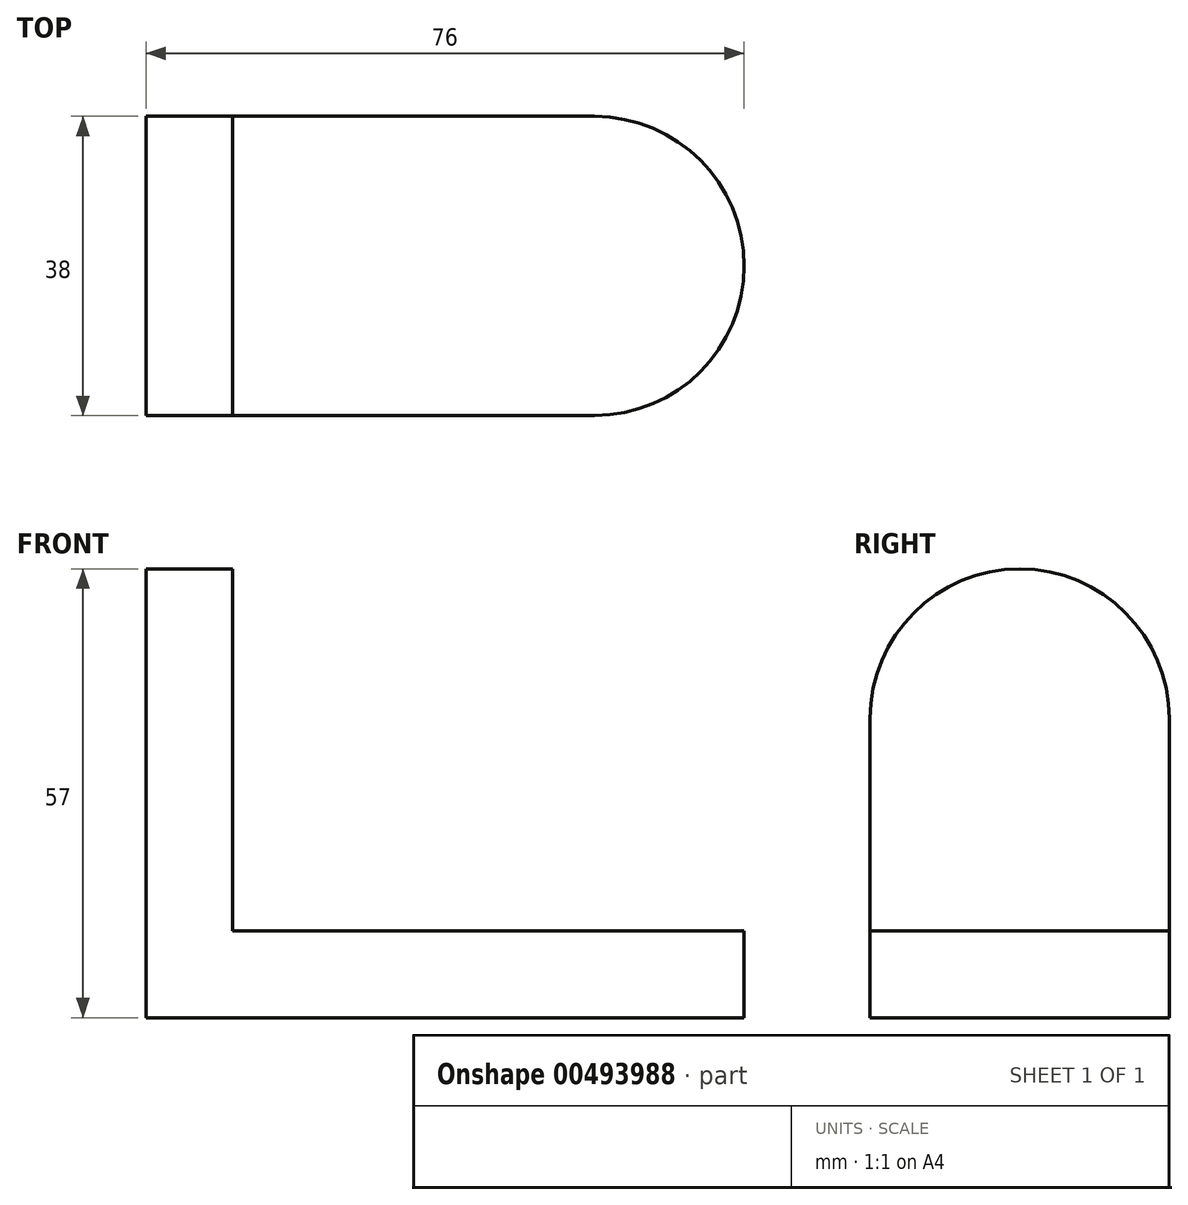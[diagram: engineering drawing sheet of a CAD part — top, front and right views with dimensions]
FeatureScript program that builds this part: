
annotation { "Feature Type Name" : "Feature", "Feature Type Description" : "" }
export const myFeature = defineFeature(function(context is Context, id is Id, definition is map)
    precondition{}
    {
        {
            var Q0;
            Q0=qCreatedBy(makeId("Top.planeOp"),FACE);
            var sketch = newSketch(context, id + "F0", { "sketchPlane" : qUnion([Q0])});
            skLineSegment(sketch, "E0.bottom", {"start": v(0, 0) * mm, "end": v(57, 0) * mm});
            skLineSegment(sketch, "E0.top", {"start": v(0, 38) * mm, "end": v(57, 38) * mm});
            skLineSegment(sketch, "E0.left", {"start": v(0, 0) * mm, "end": v(0, 38) * mm});
            skPoint(sketch, "E1", {"position": v(57, 19) * mm});
            skArc(sketch, "E2", {"start": v(57, 0) * mm, "mid": v(76, 19) * mm, "end": v(57, 38) * mm});
            skSolve(sketch);
        }
        {
            var Q0;
            Q0=makeQuery(id+"F0.imprint","IMPRINT",FACE,{"disambiguationData":[TD([[makeQuery(id+"F0.imprint","IMPRINT",EDGE,{"derivedFrom":sQuery(id+"F0.wireOp",EDGE,"E0.bottom")}),1.0]])]});
            extrude(context, id + "F1", {"entities" : qUnion([Q0]), "depth" : 11 * mm});
        }
        {
            var Q0;
            Q0=qCreatedBy(makeId("Right.planeOp"),FACE);
            var sketch = newSketch(context, id + "F2", { "sketchPlane" : qUnion([Q0])});
            skLineSegment(sketch, "E3.bottom", {"start": v(0, 0) * mm, "end": v(38, 0) * mm});
            skLineSegment(sketch, "E3.left", {"start": v(0, 0) * mm, "end": v(0, 38) * mm});
            skLineSegment(sketch, "E3.right", {"start": v(38, 0) * mm, "end": v(38, 38) * mm});
            skPoint(sketch, "E4", {"position": v(19, 38) * mm});
            skArc(sketch, "E5", {"start": v(38, 38) * mm, "mid": v(19, 57) * mm, "end": v(0, 38) * mm});
            skSolve(sketch);
        }
        {
            var Q0;
            Q0=makeQuery(id+"F2.imprint","IMPRINT",FACE,{"disambiguationData":[TD([[makeQuery(id+"F2.imprint","IMPRINT",EDGE,{"derivedFrom":sQuery(id+"F2.wireOp",EDGE,"E3.bottom")}),1.0]])]});
            extrude(context, id + "F3", {"entities" : qUnion([Q0]), "operationType" : NewBodyOperationType.ADD, "depth" : 11 * mm});
        }
    });
